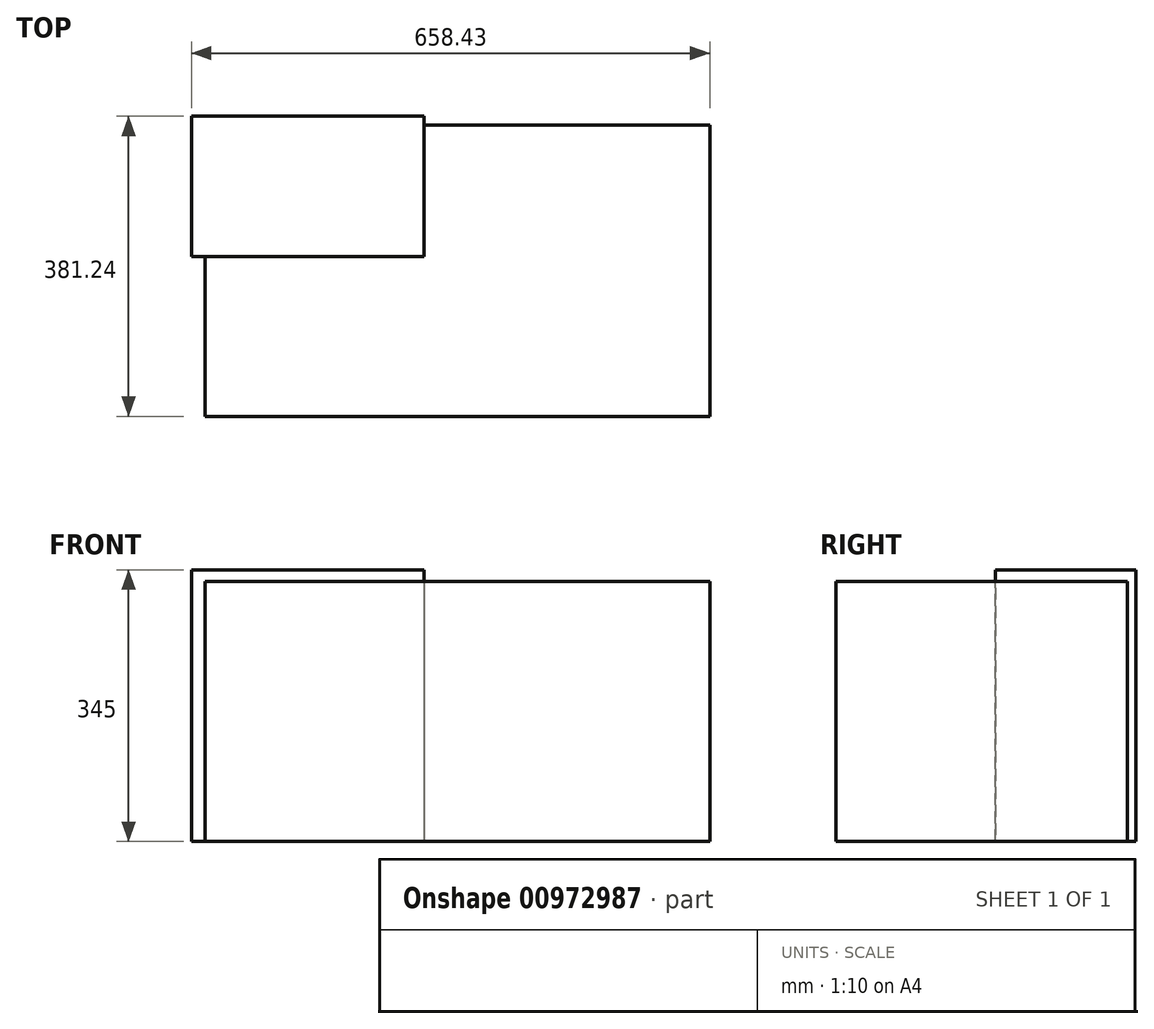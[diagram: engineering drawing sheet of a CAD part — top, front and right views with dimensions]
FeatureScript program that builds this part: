
annotation { "Feature Type Name" : "Feature", "Feature Type Description" : "" }
export const myFeature = defineFeature(function(context is Context, id is Id, definition is map)
    precondition{}
    {
        {
            var Q0;
            Q0=qCreatedBy(makeId("Top.planeOp"),FACE);
            var sketch = newSketch(context, id + "F0", { "sketchPlane" : qUnion([Q0])});
            skLineSegment(sketch, "E0.bottom", {"start": v(-95.77, 52.11) * mm, "end": v(199.6, 52.11) * mm});
            skLineSegment(sketch, "E0.top", {"start": v(-95.77, -126.1) * mm, "end": v(199.6, -126.1) * mm});
            skLineSegment(sketch, "E0.left", {"start": v(-95.77, 52.11) * mm, "end": v(-95.77, -126.1) * mm});
            skLineSegment(sketch, "E0.right", {"start": v(199.6, 52.11) * mm, "end": v(199.6, -126.1) * mm});
            skSolve(sketch);
        }
        {
            var Q0;
            Q0=qCreatedBy(makeId("Top.planeOp"),FACE);
            var sketch = newSketch(context, id + "F1", { "sketchPlane" : qUnion([Q0])});
            skLineSegment(sketch, "E1.bottom", {"start": v(-78.22, 41.05) * mm, "end": v(562.66, 41.05) * mm});
            skLineSegment(sketch, "E1.top", {"start": v(-78.22, -329.13) * mm, "end": v(562.66, -329.13) * mm});
            skLineSegment(sketch, "E1.left", {"start": v(-78.22, 41.05) * mm, "end": v(-78.22, -329.13) * mm});
            skLineSegment(sketch, "E1.right", {"start": v(562.66, 41.05) * mm, "end": v(562.66, -329.13) * mm});
            skSolve(sketch);
        }
        {
            var Q0;
            Q0=makeQuery(id+"F1.imprint","IMPRINT",FACE,{"disambiguationData":[TD([[makeQuery(id+"F1.imprint","IMPRINT",EDGE,{"derivedFrom":sQuery(id+"F1.wireOp",EDGE,"E1.bottom")}),-1.0]])]});
            extrude(context, id + "F2", {"entities" : qUnion([Q0]), "depth" : 330 * mm, "offsetDistance" : 25 * mm});
        }
        {
            var Q0;
            Q0=makeQuery(id+"F0.imprint","IMPRINT",FACE,{"disambiguationData":[TD([[makeQuery(id+"F0.imprint","IMPRINT",EDGE,{"derivedFrom":sQuery(id+"F0.wireOp",EDGE,"E0.bottom")}),-1.0]])]});
            extrude(context, id + "F3", {"entities" : qUnion([Q0]), "operationType" : NewBodyOperationType.ADD, "depth" : 345 * mm, "offsetDistance" : 25 * mm});
        }
    });
